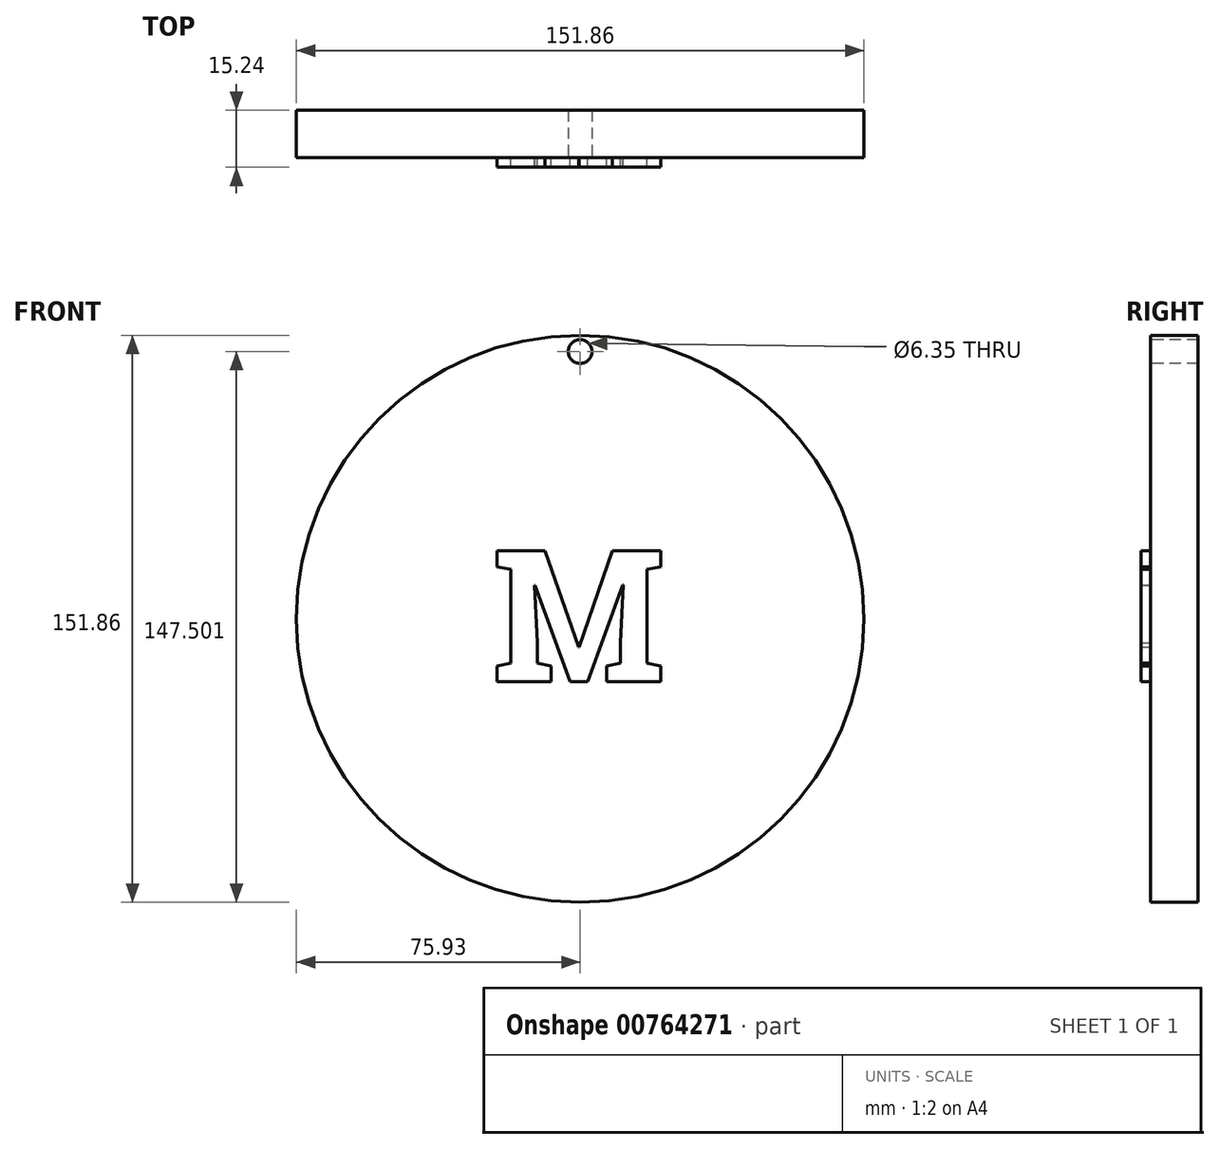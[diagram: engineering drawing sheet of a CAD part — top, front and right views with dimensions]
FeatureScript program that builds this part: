
annotation { "Feature Type Name" : "Feature", "Feature Type Description" : "" }
export const myFeature = defineFeature(function(context is Context, id is Id, definition is map)
    precondition{}
    {
        {
            var Q0;
            Q0=qCreatedBy(makeId("Front.planeOp"),FACE);
            var sketch = newSketch(context, id + "F0", { "sketchPlane" : qUnion([Q0])});
            skCircle(sketch, "E0", {"center": v(0, 0) * mm, "radius": 75.93 * mm});
            skSolve(sketch);
        }
        {
            var Q0;
            Q0=makeQuery(id+"F0.imprint","IMPRINT",FACE,{"disambiguationData":[TD([[makeQuery(id+"F0.imprint","IMPRINT",EDGE,{"derivedFrom":sQuery(id+"F0.wireOp",EDGE,"E0")}),1.0]])]});
            extrude(context, id + "F1", {"entities" : qUnion([Q0]), "depth" : 12.7 * mm, "offsetDistance" : 25.4 * mm});
        }
        {
            var Q0;
            Q0=makeQuery(id+"F1.opExtrude","CAP_FACE",FACE,{"disambiguationData":[OSD([sQuery(id+"F0.wireOp",EDGE,"E0")])],"isStart":false});
            var sketch = newSketch(context, id + "F2", { "sketchPlane" : qUnion([Q0])});
            skCircle(sketch, "E1", {"center": v(0, 71.57) * mm, "radius": 3.35 * mm});
            skSolve(sketch);
        }
        {
            var Q0;
            Q0=sQuery(id+"F2.wireOp",VERTEX,"E1.center");
            var Q1;
            Q1=makeQuery(id+"F1.opExtrude","SWEPT_BODY",BODY,{"disambiguationData":[OSD([sQuery(id+"F0.wireOp",EDGE,"E0")])]});
            hole(context, id + "F3", {"style" : HoleStyle.SIMPLE, "endStyle" : HoleEndStyle.THROUGH, "holeDiameter" : 6.35 * mm, "majorDiameter" : 6.35 * mm, "isTappedThrough" : true, "tappedDepth" : 12.7 * mm, "tapClearance" : 3, "locations" : qUnion([Q0]), "scope" : qUnion([Q1])});
        }
        {
            var Q0;
            Q0=makeQuery(id+"F1.opExtrude","CAP_FACE",FACE,{"disambiguationData":[OSD([sQuery(id+"F0.wireOp",EDGE,"E0")])],"isStart":false});
            var sketch = newSketch(context, id + "F4", { "sketchPlane" : qUnion([Q0])});
            skText(sketch, "E2", { "text": "M", "fontName": "RobotoSlab-Bold.ttf"});
            const initialGuessF4  = {"E2": [-0.02359, -0.0168, 1, 0, 0.03541]};
            skSetInitialGuess(sketch, initialGuessF4);
            skSolve(sketch);
        }
        {
            var Q0;
            Q0 = qSketchRegion(id + "F4", true);
            extrude(context, id + "F5", {"entities" : qUnion([Q0]), "operationType" : NewBodyOperationType.ADD, "depth" : 2.54 * mm, "offsetDistance" : 25.4 * mm});
        }
    });
